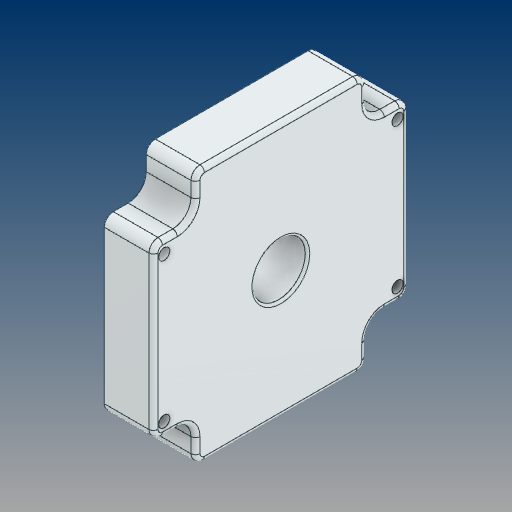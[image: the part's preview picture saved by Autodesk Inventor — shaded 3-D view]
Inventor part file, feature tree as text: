
AUTODESK INVENTOR PART (.ipt)
format: ipt  version: 2021 (Build 250183000, 183)  size: 173,568 bytes
history: native  units: mm
features: fillet x1
ambient origin geometry x8: Origin, YZ Plane, XZ Plane, XY Plane, X Axis, Y Axis, Z Axis, Center Point
bodies: Solid1 (feature_tree)
feature tree (1):
  fillet  "Fillet2"  [1 undecoded]
note: 1 required parameter value undecoded (feature->parameter linkage not recoverable at this tier; creation-order binding heuristic only, values carry confidence <= 0.55)
